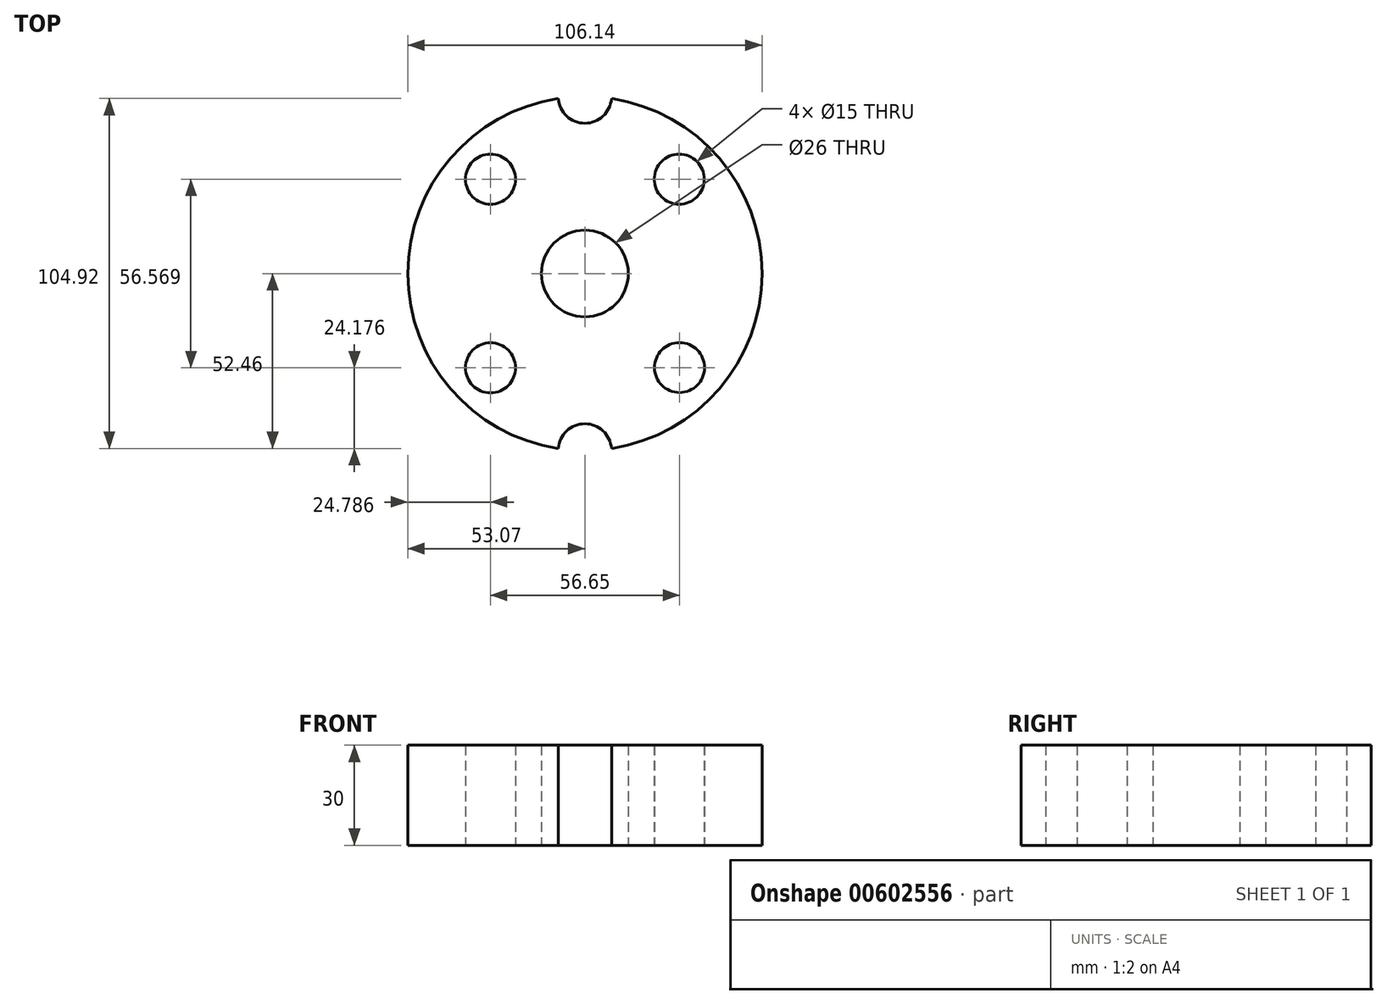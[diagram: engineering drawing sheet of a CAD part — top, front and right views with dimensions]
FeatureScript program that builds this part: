
annotation { "Feature Type Name" : "Feature", "Feature Type Description" : "" }
export const myFeature = defineFeature(function(context is Context, id is Id, definition is map)
    precondition{}
    {
        {
            var Q0;
            Q0=qCreatedBy(makeId("Top.planeOp"),FACE);
            var sketch = newSketch(context, id + "F0", { "sketchPlane" : qUnion([Q0])});
            skArc(sketch, "E0", {"start": v(-7.98, 52.46) * mm, "mid": v(-53.07, 0) * mm, "end": v(-7.98, -52.46) * mm});
            skPoint(sketch, "E1.start.orphan", {"position": v(0, 53.07) * mm});
            skPoint(sketch, "E2.start.orphan", {"position": v(0, -53.07) * mm});
            skCircle(sketch, "E3", {"center": v(0, 0) * mm, "radius": 13 * mm});
            skCircle(sketch, "E4", {"center": v(0, 0) * mm, "radius": 25 * mm});
            skArc(sketch, "E5", {"start": v(33.13, -22.41) * mm, "mid": v(40, 0.06) * mm, "end": v(33.07, 22.5) * mm});
            skCircle(sketch, "E6", {"center": v(28.28, 28.28) * mm, "radius": 7.5 * mm});
            skCircle(sketch, "E7", {"center": v(-28.28, 28.28) * mm, "radius": 7.5 * mm});
            skCircle(sketch, "E8", {"center": v(-28.28, -28.28) * mm, "radius": 7.5 * mm});
            skCircle(sketch, "E9", {"center": v(28.37, -28.2) * mm, "radius": 7.5 * mm});
            skArc(sketch, "E10.trimOffspring", {"start": v(22.5, 33.07) * mm, "mid": v(0, 40) * mm, "end": v(-22.5, 33.07) * mm});
            skArc(sketch, "E11.trimOffspring", {"start": v(-33.07, 22.5) * mm, "mid": v(-40, 0) * mm, "end": v(-33.07, -22.5) * mm});
            skArc(sketch, "E12.trimOffspring", {"start": v(-22.5, -33.07) * mm, "mid": v(0.06, -40) * mm, "end": v(22.6, -33) * mm});
            skArc(sketch, "E13", {"start": v(-7.98, 52.46) * mm, "mid": v(0, 45.07) * mm, "end": v(7.98, 52.46) * mm});
            skArc(sketch, "E14", {"start": v(7.98, -52.46) * mm, "mid": v(0, -45.07) * mm, "end": v(-7.98, -52.46) * mm});
            skArc(sketch, "E15.trimOffspring", {"start": v(7.98, -52.46) * mm, "mid": v(53.07, 0) * mm, "end": v(7.98, 52.46) * mm});
            skSolve(sketch);
        }
        {
            var Q0;
            Q0 = qSketchRegion(id + "F0", true);
            var Q1;
            Q1=makeQuery(id+"F0.imprint","IMPRINT",FACE,{"disambiguationData":[TD([[makeQuery(id+"F0.imprint","IMPRINT",EDGE,{"derivedFrom":sQuery(id+"F0.wireOp",EDGE,"E4")}),-1.0]])]});
            var Q2;
            Q2=makeQuery(id+"F0.imprint","IMPRINT",FACE,{"disambiguationData":[TD([[makeQuery(id+"F0.imprint","IMPRINT",EDGE,{"derivedFrom":sQuery(id+"F0.wireOp",EDGE,"E3")}),-1.0]])]});
            extrude(context, id + "F1", {"entities" : qUnion([Q0, Q1, Q2]), "depth" : 30 * mm, "offsetDistance" : 25 * mm});
        }
    });
